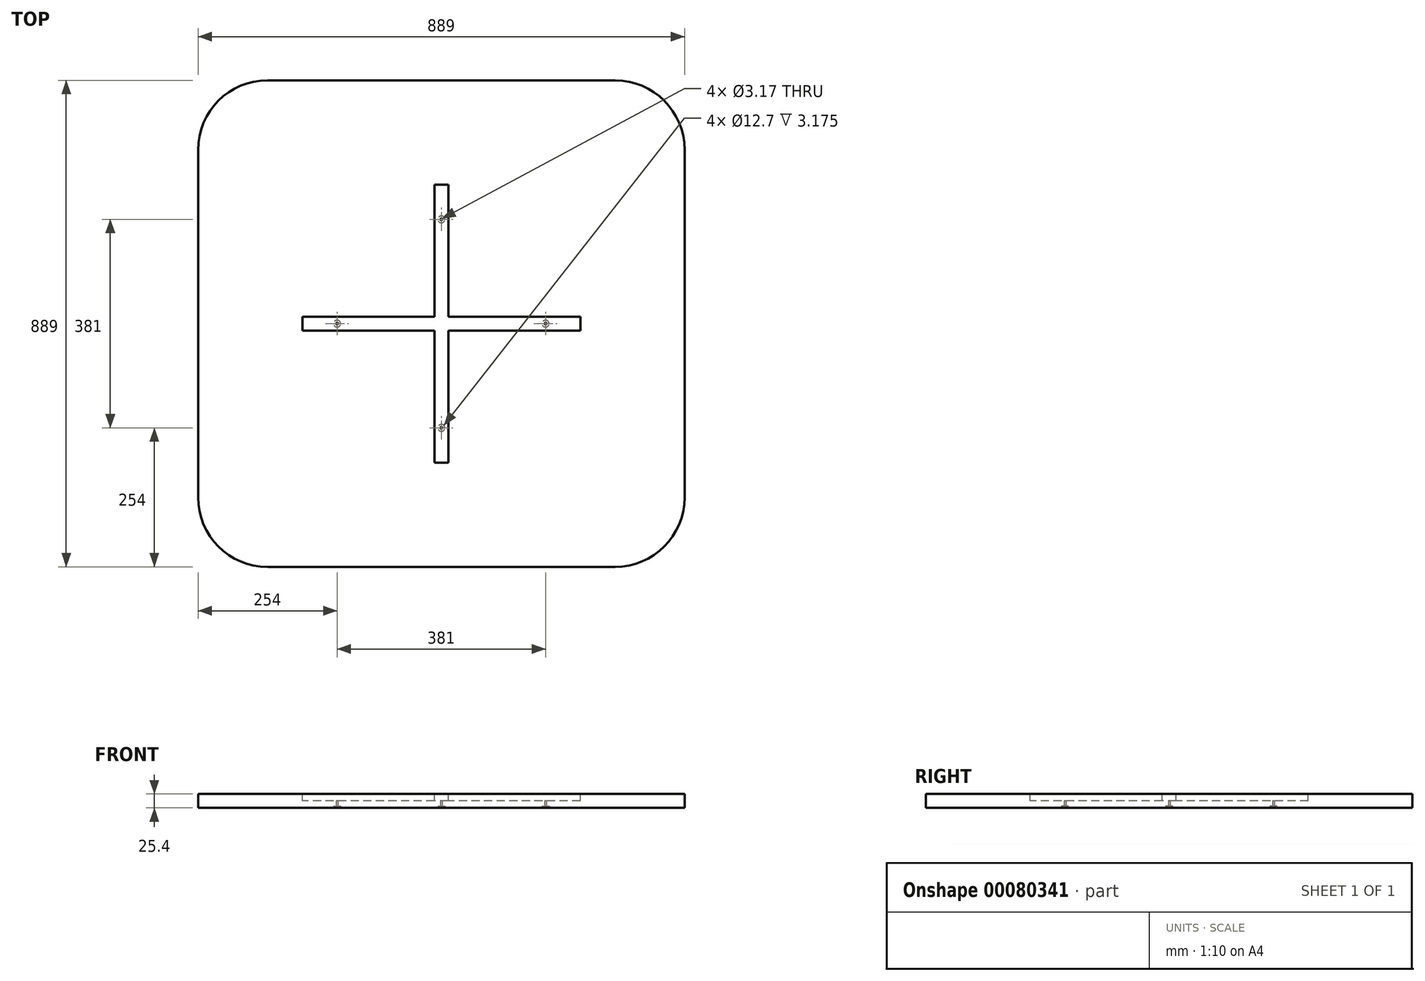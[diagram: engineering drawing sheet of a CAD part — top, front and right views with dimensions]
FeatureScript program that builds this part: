
annotation { "Feature Type Name" : "Feature", "Feature Type Description" : "" }
export const myFeature = defineFeature(function(context is Context, id is Id, definition is map)
    precondition{}
    {
        {
            var Q0;
            Q0=qCreatedBy(makeId("Top.planeOp"),FACE);
            var sketch = newSketch(context, id + "F0", { "sketchPlane" : qUnion([Q0])});
            skLineSegment(sketch, "E0.bottom", {"start": v(444.5, 444.5) * mm, "end": v(-444.5, 444.5) * mm});
            skLineSegment(sketch, "E0.top", {"start": v(444.5, -444.5) * mm, "end": v(-444.5, -444.5) * mm});
            skLineSegment(sketch, "E0.left", {"start": v(444.5, 444.5) * mm, "end": v(444.5, -444.5) * mm});
            skLineSegment(sketch, "E0.right", {"start": v(-444.5, 444.5) * mm, "end": v(-444.5, -444.5) * mm});
            skPoint(sketch, "E0.middle", {"position": v(0, 0) * mm});
            skSolve(sketch);
        }
        {
            var Q0;
            Q0=makeQuery(id+"F0.imprint","IMPRINT",FACE,{"disambiguationData":[TD([[makeQuery(id+"F0.imprint","IMPRINT",EDGE,{"derivedFrom":sQuery(id+"F0.wireOp",EDGE,"E0.bottom")}),1.0]])]});
            extrude(context, id + "F1", {"entities" : qUnion([Q0]), "depth" : 25.4 * mm});
        }
        {
            var Q0;
            Q0=makeQuery(id+"F1.opExtrude","CAP_FACE",FACE,{"disambiguationData":[OSD([sQuery(id+"F0.wireOp",EDGE,"E0.bottom"),sQuery(id+"F0.wireOp",EDGE,"E0.top"),sQuery(id+"F0.wireOp",EDGE,"E0.left"),sQuery(id+"F0.wireOp",EDGE,"E0.right")])],"isStart":false});
            var sketch = newSketch(context, id + "F5", { "sketchPlane" : qUnion([Q0])});
            skLineSegment(sketch, "E1.bottom", {"start": v(12.7, 254) * mm, "end": v(-12.7, 254) * mm});
            skLineSegment(sketch, "E1.top", {"start": v(12.7, -254) * mm, "end": v(-12.7, -254) * mm});
            skLineSegment(sketch, "E1.left", {"start": v(12.7, 254) * mm, "end": v(12.7, 12.7) * mm});
            skLineSegment(sketch, "E1.right", {"start": v(-12.7, 254) * mm, "end": v(-12.7, 12.7) * mm});
            skPoint(sketch, "E1.middle", {"position": v(0, 0) * mm});
            skLineSegment(sketch, "E2.bottom", {"start": v(254, 12.7) * mm, "end": v(12.7, 12.7) * mm});
            skLineSegment(sketch, "E2.top", {"start": v(254, -12.7) * mm, "end": v(12.7, -12.7) * mm});
            skLineSegment(sketch, "E2.left", {"start": v(254, 12.7) * mm, "end": v(254, -12.7) * mm});
            skLineSegment(sketch, "E2.right", {"start": v(-254, 12.7) * mm, "end": v(-254, -12.7) * mm});
            skLineSegment(sketch, "E3.trimOffspring", {"start": v(12.7, -12.7) * mm, "end": v(12.7, -254) * mm});
            skLineSegment(sketch, "E4.trimOffspring", {"start": v(-12.7, 12.7) * mm, "end": v(-254, 12.7) * mm});
            skLineSegment(sketch, "E5.trimOffspring", {"start": v(-12.7, -12.7) * mm, "end": v(-12.7, -254) * mm});
            skLineSegment(sketch, "E6.trimOffspring", {"start": v(-12.7, -12.7) * mm, "end": v(-254, -12.7) * mm});
            skSolve(sketch);
        }
        {
            var Q0;
            Q0 = qSketchRegion(id + "F5", true);
            extrude(context, id + "F6", {"entities" : qUnion([Q0]), "operationType" : NewBodyOperationType.REMOVE, "oppositeDirection" : true, "depth" : 12.7 * mm});
        }
        {
            var Q0;
            Q0=makeQuery(id+"F1.opExtrude","CAP_FACE",FACE,{"disambiguationData":[OSD([sQuery(id+"F0.wireOp",EDGE,"E0.bottom"),sQuery(id+"F0.wireOp",EDGE,"E0.top"),sQuery(id+"F0.wireOp",EDGE,"E0.left"),sQuery(id+"F0.wireOp",EDGE,"E0.right")])],"isStart":true});
            var sketch = newSketch(context, id + "F2", { "sketchPlane" : qUnion([Q0])});
            skPoint(sketch, "E7", {"position": v(190.5, 0) * mm});
            skPoint(sketch, "E8", {"position": v(-190.5, 0) * mm});
            skPoint(sketch, "E9", {"position": v(0, 190.5) * mm});
            skPoint(sketch, "E10", {"position": v(0, -190.5) * mm});
            skSolve(sketch);
        }
        {
            var Q0;
            Q0=sQuery(id+"F2.wireOp",VERTEX,"E8");
            var Q1;
            Q1=sQuery(id+"F2.wireOp",VERTEX,"E9");
            var Q2;
            Q2=sQuery(id+"F2.wireOp",VERTEX,"E7");
            var Q3;
            Q3=sQuery(id+"F2.wireOp",VERTEX,"E10");
            var Q4;
            Q4=makeQuery(id+"F1.opExtrude","SWEPT_BODY",BODY,{"disambiguationData":[OSD([sQuery(id+"F0.wireOp",EDGE,"E0.bottom"),sQuery(id+"F0.wireOp",EDGE,"E0.top"),sQuery(id+"F0.wireOp",EDGE,"E0.left"),sQuery(id+"F0.wireOp",EDGE,"E0.right")])]});
            hole(context, id + "F3", {"style" : HoleStyle.C_BORE, "endStyle" : HoleEndStyle.BLIND, "holeDiameter" : 3.17 * mm, "cBoreDiameter" : 12.7 * mm, "cBoreDepth" : 3.17 * mm, "holeDepth" : 63.5 * mm, "locations" : qUnion([Q0, Q1, Q2, Q3]), "scope" : qUnion([Q4])});
        }
        {
            var Q0;
            Q0=makeQuery(id+"F1.opExtrude","SWEPT_EDGE",EDGE,{"disambiguationData":[OSD([sQuery(id+"F0.wireOp",EDGE,"E0.top"),sQuery(id+"F0.wireOp",EDGE,"E0.left")])]});
            var Q1;
            Q1=makeQuery(id+"F1.opExtrude","SWEPT_EDGE",EDGE,{"disambiguationData":[OSD([sQuery(id+"F0.wireOp",EDGE,"E0.bottom"),sQuery(id+"F0.wireOp",EDGE,"E0.left")])]});
            var Q2;
            Q2=makeQuery(id+"F1.opExtrude","SWEPT_EDGE",EDGE,{"disambiguationData":[OSD([sQuery(id+"F0.wireOp",EDGE,"E0.bottom"),sQuery(id+"F0.wireOp",EDGE,"E0.right")])]});
            var Q3;
            Q3=makeQuery(id+"F1.opExtrude","SWEPT_EDGE",EDGE,{"disambiguationData":[OSD([sQuery(id+"F0.wireOp",EDGE,"E0.top"),sQuery(id+"F0.wireOp",EDGE,"E0.right")])]});
            fillet(context, id + "F4", {"entities" : qUnion([Q0, Q1, Q2, Q3]), "radius" : 127 * mm, "tangentPropagation" : true, "allowEdgeOverflow" : false});
        }
    });
